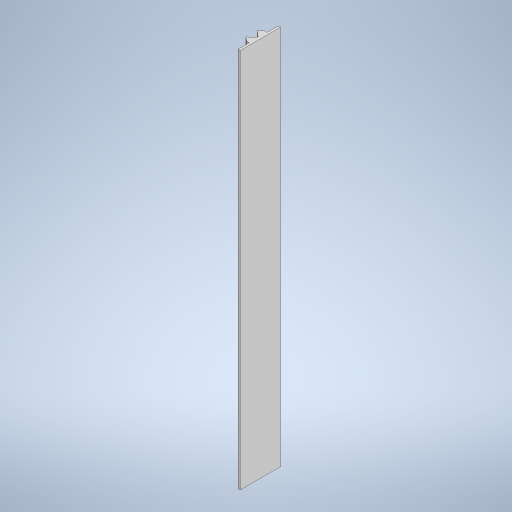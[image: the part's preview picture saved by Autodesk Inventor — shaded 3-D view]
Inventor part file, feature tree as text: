
AUTODESK INVENTOR PART (.ipt)
format: ipt  version: 2024 (Build 280153000, 153)  size: 258,048 bytes
history: native  units: mm
features: extrude x2, chamfer x2, sketch x2
ambient origin geometry x8: Origin, YZ Plane, XZ Plane, XY Plane, X Axis, Y Axis, Z Axis, Center Point
bodies: Solid1 (feature_tree)
feature tree (6):
  extrude  "Extrusion1"  Depth=2.0mm TaperAngle=45.0deg
  chamfer  "Chamfer1"  Distance=2.0mm Angle=45.0deg
  chamfer  "Chamfer2"  Distance=1000.0mm
  extrude  "Extrusion2"  [1 undecoded]
  sketch  "Sketch1"  dims[d1=340.0mm d2=0.0mm d3=0.1mm d4=2.0mm d5=45.0deg d6=1.0mm d7=2.0mm d8=45.0deg d9=1000.0mm d10=0.0mm]
  sketch  "Sketch2"
note: 1 required parameter value undecoded (feature->parameter linkage not recoverable at this tier; creation-order binding heuristic only, values carry confidence <= 0.55)
